# Revit family: Receptor_Sani-Flor_12_Inch_Round_8_Inch_Sump-Zurn-Z1950
name_source: partatom
category: Plumbing Fixtures
units: mm (PartAtom-declared; Revit-internal decimal feet)

## family parameters
Always vertical = Yes
Cut with Voids When Loaded = No
Maintain Annotation Orientation = No
OmniClass Number = 23.45.05.14.14
OmniClass Title = Sinks/Lavatories
Part Type = Normal
Room Calculation Point = No
Round Connector Dimension = Use Radius
Shared = No
Work Plane-Based = No

## types (16) — shared parameters
Approx. Weight (Lbs) = 34 "
Assembly Code = D2030300
CW Connection = No
Default Elevation = 4 "
Description = 12 [305] DIAMETER A.R.E. SANI-FLOR RECEPTOR 8 [203] SUMP DEPTH
Grate Open Area (Sq. In) = 22
HW Connection = No
Main Material = Iron - Zurn - Cast - White A.R.E Coated - Interior
Manufacturer = Zurn Water, LLC
Manufacurer Brand = Zurn
Modified Date = 12/26/2025
Product Documentation Link = https://files.zurn.com
Product Page URL = https://www.zurn.com
Product data url = https://www.bimobject.com
Thickness = 0.25 "
Trap Primer = No
URL = www.zurn.com
Vent Connection = No
WFU = 1
Waste Connection = Yes
zero-valued in all types: CWFU, HWFU

## per-type parameters (varying)
| type | A_ Pipe Size (Actual-Inner) | A_ Pipe Size (Actual-Outer) | A_ Pipe Size (Nominal) | Connector Radius | E_ Body Height | E_ Body Length_Derived | Grate Material | Model | Type Comments | ZN Top | ZN Top height |
| Z1950-3IC | 3.068 " | 3.5 " | 3 " | 1.5 " | 10.625 " | 10.625 " | Iron - Zurn - Cast - White A.R.E Coated - Interior | Z1950 | Z1950 Sani-Flor Receptor 3 Inch Inside Caulk Outlet | No | 0 " |
| Z1950-4IC | 4.026 " | 4.5 " | 4 " | 2 " | 10.625 " | 10.625 " | Iron - Zurn - Cast - White A.R.E Coated - Interior | Z1950 | Z1950 Sani-Flor Receptor 4 Inch Inside Caulk Outlet | No | 0 " |
| Z1950-2NH | 2.067 " | 2.375 " | 2 " | 1 " | 10.625 " | 10.625 " | Iron - Zurn - Cast - White A.R.E Coated - Interior | Z1950 | Z1950 Sani-Flor Receptor 2 Inch No-Hub Outlet | No | 0 " |
| Z1950-3NH | 3.068 " | 3.5 " | 3 " | 1.5 " | 10.625 " | 10.625 " | Iron - Zurn - Cast - White A.R.E Coated - Interior | Z1950 | Z1950 Sani-Flor Receptor 3 Inch No-Hub Outlet | No | 0 " |
| Z1950-4NH | 4.026 " | 4.5 " | 4 " | 2 " | 10.625 " | 10.625 " | Iron - Zurn - Cast - White A.R.E Coated - Interior | Z1950 | Z1950 Sani-Flor Receptor 4 Inch No-Hub Outlet | No | 0 " |
| Z1950-2NL | 2.067 " | 2.375 " | 2 " | 1 " | 10 " | 10 " | Iron - Zurn - Cast - White A.R.E Coated - Interior | Z1950 | Z1950 Sani-Flor Receptor 2 Inch Neo-Loc Outlet | No | 0 " |
| Z1950-3NL | 3.068 " | 3.5 " | 3 " | 1.5 " | 10 " | 10 " | Iron - Zurn - Cast - White A.R.E Coated - Interior | Z1950 | Z1950 Sani-Flor Receptor 3 Inch Neo-Loc Outlet | No | 0 " |
| Z1950-4NL | 4.026 " | 4.5 " | 4 " | 2 " | 10 " | 10 " | Iron - Zurn - Cast - White A.R.E Coated - Interior | Z1950 | Z1950 Sani-Flor Receptor 4 Inch Neo-Loc Outlet | No | 0 " |
| ZN1950-3IC | 3.068 " | 3.5 " | 3 " | 1.5 " | 11 " | 10.625 " | Bronze - Zurn - Polished Nickel | ZN1950 | ZN1950 Sani-Flor Receptor 3 Inch Inside Caulk Outlet | Yes | 0.375 " |
| ZN1950-4IC | 4.026 " | 4.5 " | 4 " | 2 " | 11 " | 10.625 " | Bronze - Zurn - Polished Nickel | ZN1950 | ZN1950 Sani-Flor Receptor 4 Inch Inside Caulk Outlet | Yes | 0.375 " |
| ZN1950-2NH | 2.067 " | 2.375 " | 2 " | 1 " | 11 " | 10.625 " | Bronze - Zurn - Polished Nickel | ZN1950 | ZN1950 Sani-Flor Receptor 2 Inch No-Hub Outlet | Yes | 0.375 " |
| ZN1950-3NH | 3.068 " | 3.5 " | 3 " | 1.5 " | 11 " | 10.625 " | Bronze - Zurn - Polished Nickel | ZN1950 | ZN1950 Sani-Flor Receptor 3 Inch No-Hub Outlet | Yes | 0.375 " |
| ZN1950-4NH | 4.026 " | 4.5 " | 4 " | 2 " | 11 " | 10.625 " | Bronze - Zurn - Polished Nickel | ZN1950 | ZN1950 Sani-Flor Receptor 4 Inch No-Hub Outlet | Yes | 0.375 " |
| ZN1950-2NL | 2.067 " | 2.375 " | 2 " | 1 " | 10.375 " | 10 " | Bronze - Zurn - Polished Nickel | ZN1950 | ZN1950 Sani-Flor Receptor 2 Inch Neo-Loc Outlet | Yes | 0.375 " |
| ZN1950-3NL | 3.068 " | 3.5 " | 3 " | 1.5 " | 10.375 " | 10 " | Bronze - Zurn - Polished Nickel | ZN1950 | ZN1950 Sani-Flor Receptor 3 Inch Neo-Loc Outlet | Yes | 0.375 " |
| ZN1950-4NL | 4.026 " | 4.5 " | 4 " | 2 " | 10.375 " | 10 " | Bronze - Zurn - Polished Nickel | ZN1950 | ZN1950 Sani-Flor Receptor 4 Inch Neo-Loc Outlet | Yes | 0.375 " |

## geometry (parser evidence)
native form markers: Blend x12, Sweep x3
no freeform markers — native parametric forms only
